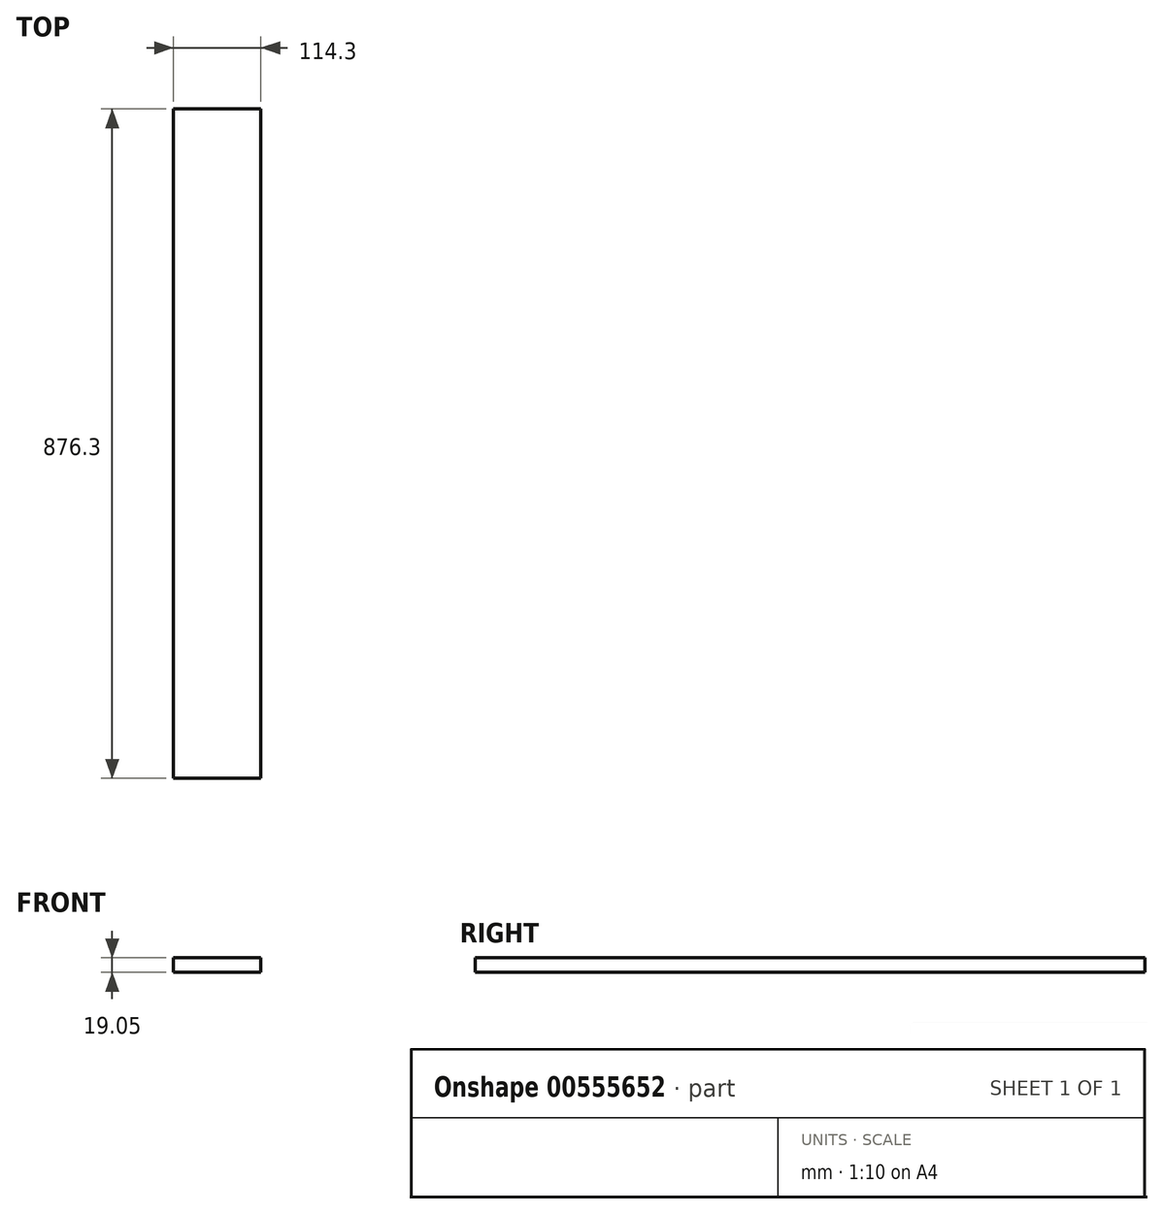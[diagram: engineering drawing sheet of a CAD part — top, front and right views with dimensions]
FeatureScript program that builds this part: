
annotation { "Feature Type Name" : "Feature", "Feature Type Description" : "" }
export const myFeature = defineFeature(function(context is Context, id is Id, definition is map)
    precondition{}
    {
        {
            var Q0;
            Q0=qCreatedBy(makeId("Top.planeOp"),FACE);
            var sketch = newSketch(context, id + "F0", { "sketchPlane" : qUnion([Q0])});
            skLineSegment(sketch, "E0.bottom", {"start": v(57.15, 438.15) * mm, "end": v(-57.15, 438.15) * mm});
            skLineSegment(sketch, "E0.top", {"start": v(57.15, -438.15) * mm, "end": v(-57.15, -438.15) * mm});
            skLineSegment(sketch, "E0.left", {"start": v(57.15, 438.15) * mm, "end": v(57.15, -438.15) * mm});
            skLineSegment(sketch, "E0.right", {"start": v(-57.15, 438.15) * mm, "end": v(-57.15, -438.15) * mm});
            skPoint(sketch, "E0.middle", {"position": v(0, 0) * mm});
            skSolve(sketch);
        }
        {
            var Q0;
            Q0=makeQuery(id+"F0.imprint","IMPRINT",FACE,{"disambiguationData":[TD([[makeQuery(id+"F0.imprint","IMPRINT",EDGE,{"derivedFrom":sQuery(id+"F0.wireOp",EDGE,"E0.bottom")}),1.0]])]});
            extrude(context, id + "F1", {"entities" : qUnion([Q0]), "depth" : 19.05 * mm, "offsetDistance" : 25.4 * mm});
        }
    });
